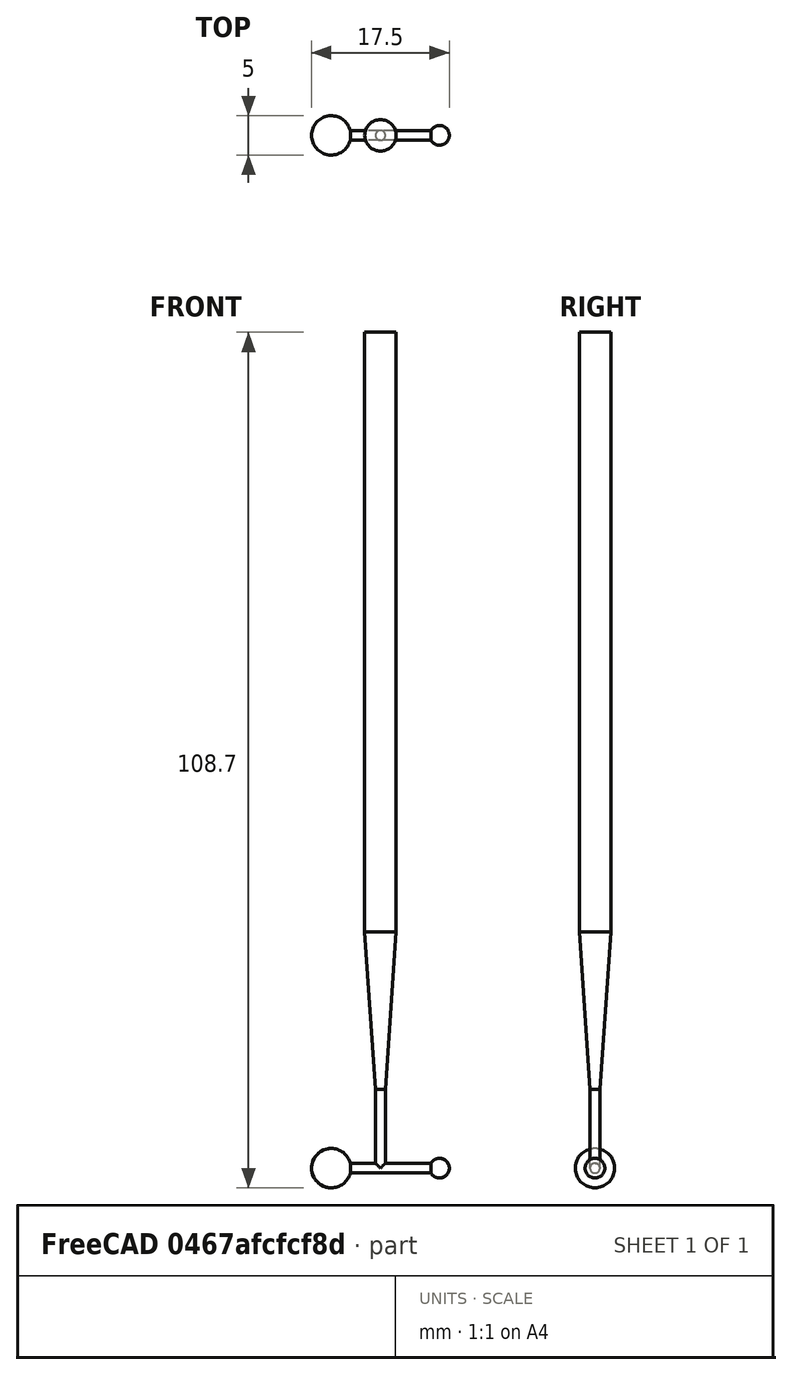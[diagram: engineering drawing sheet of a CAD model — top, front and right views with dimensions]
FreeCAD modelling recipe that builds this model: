
FCSTD DOCUMENT  (FreeCAD 0.17R13522 (Git))
Label: Camera calibration tool
License: All rights reserved
LicenseURL: http://en.wikipedia.org/wiki/All_rights_reserved
objects: Part::Cylinder×3, Part::Sphere×2, Spreadsheet::Sheet×1, Part::Cone×1, Part::MultiFuse×1
note: 7 computed .brp shape members not serialized (recipe doc carries the construction recipe); baked Part::Feature solids carry a one-line shape summary decoded from their .brp

FEATURE [Part::Sphere] Sphere
  Angle1 = -90
  Angle2 = 90
  Angle3 = 360
  AttacherType = Attacher::AttachEngine3D
  Placement = pos=(-6.25,0,0) rot=(0,0,1;0rad)
  Radius = 2.5
  expr: Placement.Base.x = -ss.D / 2 + ss.R_1
  expr: Radius = ss.R_1
FEATURE [Part::Sphere] Sphere001
  Angle1 = -90
  Angle2 = 90
  Angle3 = 360
  AttacherType = Attacher::AttachEngine3D
  Placement = pos=(7.5,0,0) rot=(0,0,1;0rad)
  Radius = 1.25
  expr: Radius = ss.R_2
  expr: Placement.Base.x = ss.D / 2 - ss.R_2
FEATURE [Part::Cylinder] Cylinder
  Angle = 360
  AttacherType = Attacher::AttachEngine3D
  Height = 13.75
  Placement = pos=(6.875,0,0) rot=(0,1,0;4.71239rad)
  Radius = 0.625
  expr: Placement.Base.x = (ss.D - ss.R_1 - ss.R_2) / 2
  expr: Height = ss.D - ss.R_1 - ss.R_2
  expr: Radius = ss.RC
FEATURE [Spreadsheet::Sheet] Spreadsheet  label="ss"
  cells = A1=R1; B1(R_1)=2.5; A2=R2; B2(R_2)=1.25; A3=D; B3(D)=17.5; A4=R_c; B4(RC)==B2 / 2
FEATURE [Part::Cylinder] Cylinder001
  Angle = 360
  AttacherType = Attacher::AttachEngine3D
  Height = 10
  Radius = 0.625
  expr: Radius = ss.RC
FEATURE [Part::Cone] Cone
  Angle = 360
  AttacherType = Attacher::AttachEngine3D
  Height = 20
  Placement = pos=(0,0,10) rot=(0,0,1;0rad)
  Radius1 = 0.625
  Radius2 = 2
  expr: Radius1 = ss.RC
FEATURE [Part::Cylinder] Cylinder002
  Angle = 360
  AttacherType = Attacher::AttachEngine3D
  Height = 76.2
  Placement = pos=(0,0,30) rot=(0,0,1;0rad)
  Radius = 2
  expr: Height = 3in
FEATURE [Part::MultiFuse] Fusion
  Shapes = -> [Sphere,Cylinder001,Cylinder002,Cone,Sphere001,Cylinder]
